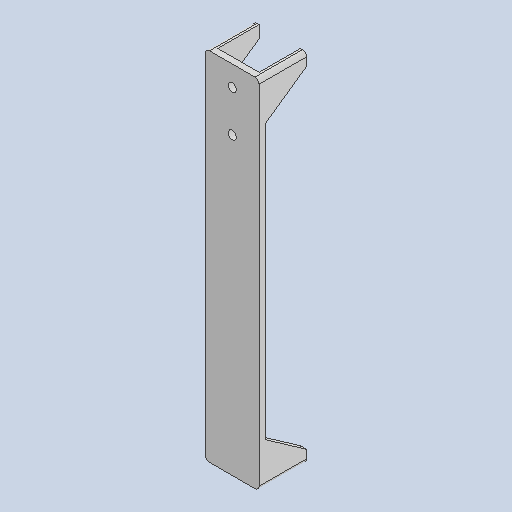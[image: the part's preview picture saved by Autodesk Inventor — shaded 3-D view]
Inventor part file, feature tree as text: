
AUTODESK INVENTOR PART (.ipt)
format: ipt  version: 2022 (Build 260153000, 153)  size: 137,216 bytes
history: native  units: mm
features: extrude x3, other x3, sketch x2, chamfer x2, reference x2, plane x1, mirror x1, fillet x1
ambient origin geometry x8: Origin, YZ Plane, XZ Plane, XY Plane, X Axis, Y Axis, Z Axis, Center Point
bodies: Solid1 (feature_tree)
feature tree (15):
  sketch  "Sketch1"  dims[d0=20.0mm d1=172.5mm]
  extrude  "Extrusion1"  Depth=172.5mm
  extrude  "Extrusion2"  Depth=3.0mm
  chamfer  "Chamfer1"  Distance=3.0mm
  chamfer  "Chamfer2"  Distance=20.0mm
  extrude  "Extrusion3"  Depth=20.0mm TaperAngle=0.0deg
  plane  "Work Plane2"
  mirror  "Mirror2"
  fillet  "Fillet1"  Radius=20.0mm
  sketch  "Sketch2"  dims[d2=3.0mm d3=3.0mm d4=3.0mm d5=0.0mm d6=20.0mm d7=20.0mm d8=0.0mm d9=20.0mm d10=2.0mm d11=6.108652mm d12=20.0mm d13=2.0mm d14=6.108652mm d15=2.0mm d16=0.0mm d17=0.0mm]
  reference  "Reference1"
  reference  "Reference2"
  parser-record x1  (decoder bookkeeping rows leaked as tree rows — omitted from the tree; the rows remain in map.json)
  other  "Bibble0.iam"
  other  "2040 Z Axis Upright:2"
note: 1 file-system path scrubbed to <path> (originals preserved in map.json)
